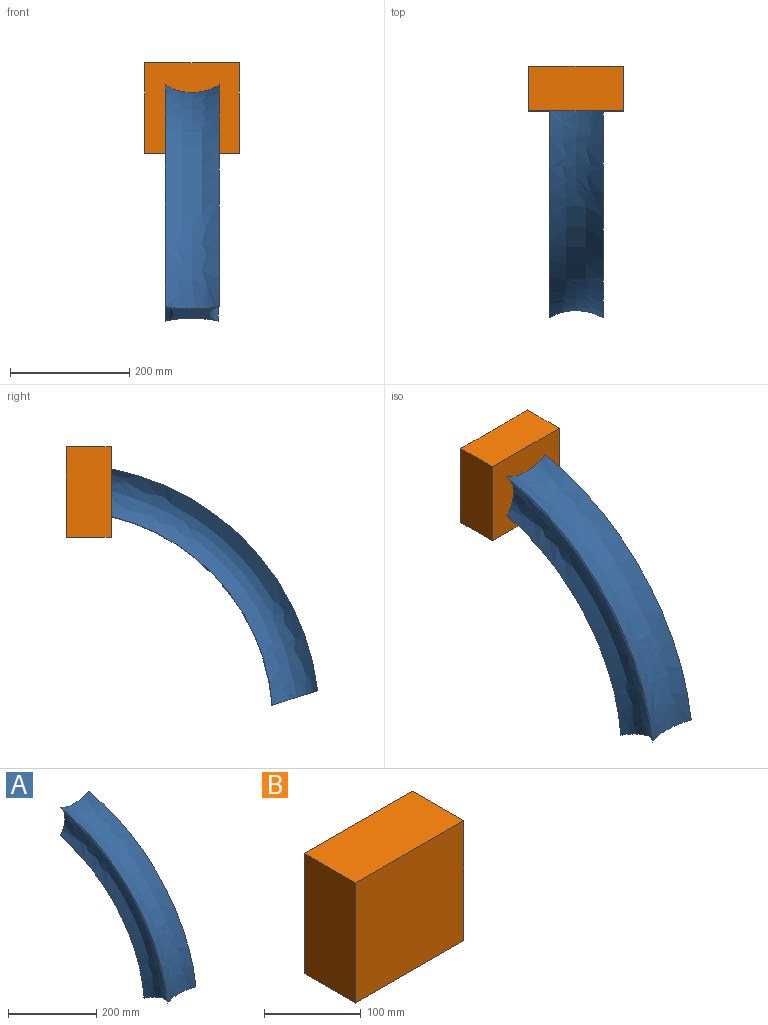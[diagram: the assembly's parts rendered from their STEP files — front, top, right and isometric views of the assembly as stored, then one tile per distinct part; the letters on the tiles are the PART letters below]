
ASSEMBLY  parts=2 mates=1
PART A: 6 faces, bbox 90.5x345.9x395.7 mm
  f0: plane 90.55x80.34mm, normal (0,1,0), area 3788mm2, adj f2,f3,f4,f5
  f1: plane 90.55x76.55mm, normal (0,-0.3,-0.95), area 3788mm2, adj f2,f3,f4,f5
  f2: bspline ~395.68x345.92mm, area 42714.1mm2, adj f0,f1,f3,f5
  f3: bspline ~376.62x345.92mm, area 50597.1mm2, adj f0,f1,f2,f4
  f4: bspline ~395.4x345.79mm, area 42511.6mm2, adj f0,f1,f3,f5
  f5: bspline ~336.52x289.55mm, area 43686.4mm2, adj f0,f1,f2,f4
PART B: 6 faces, bbox 158x75x151.8 mm
  f0: plane 151.76x75mm, normal (1,0,0), area 11381.8mm2, adj f1,f3,f4,f5
  f1: plane 157.99x75mm, normal (0,0,1), area 11849.1mm2, adj f0,f2,f4,f5
  f2: plane 151.76x75mm, normal (-1,0,0), area 11381.8mm2, adj f1,f3,f4,f5
  f3: plane 157.99x75mm, normal (0,0,-1), area 11849.1mm2, adj f0,f2,f4,f5
  f4: plane 157.99x151.76mm, normal (0,-1,0), area 23975.8mm2, adj f0,f1,f2,f3
  f5: plane 157.99x151.76mm, normal (0,1,0), area 23975.8mm2, adj f0,f1,f2,f3
PLACE A t=(-45.11,-66.03,-160.34)mm
PLACE B t=(0,8.97,184.2)mm
MATE revolute A.f0 <-> B.f4  axis (0,1,0) through (0,-66.03,184.2)mm
